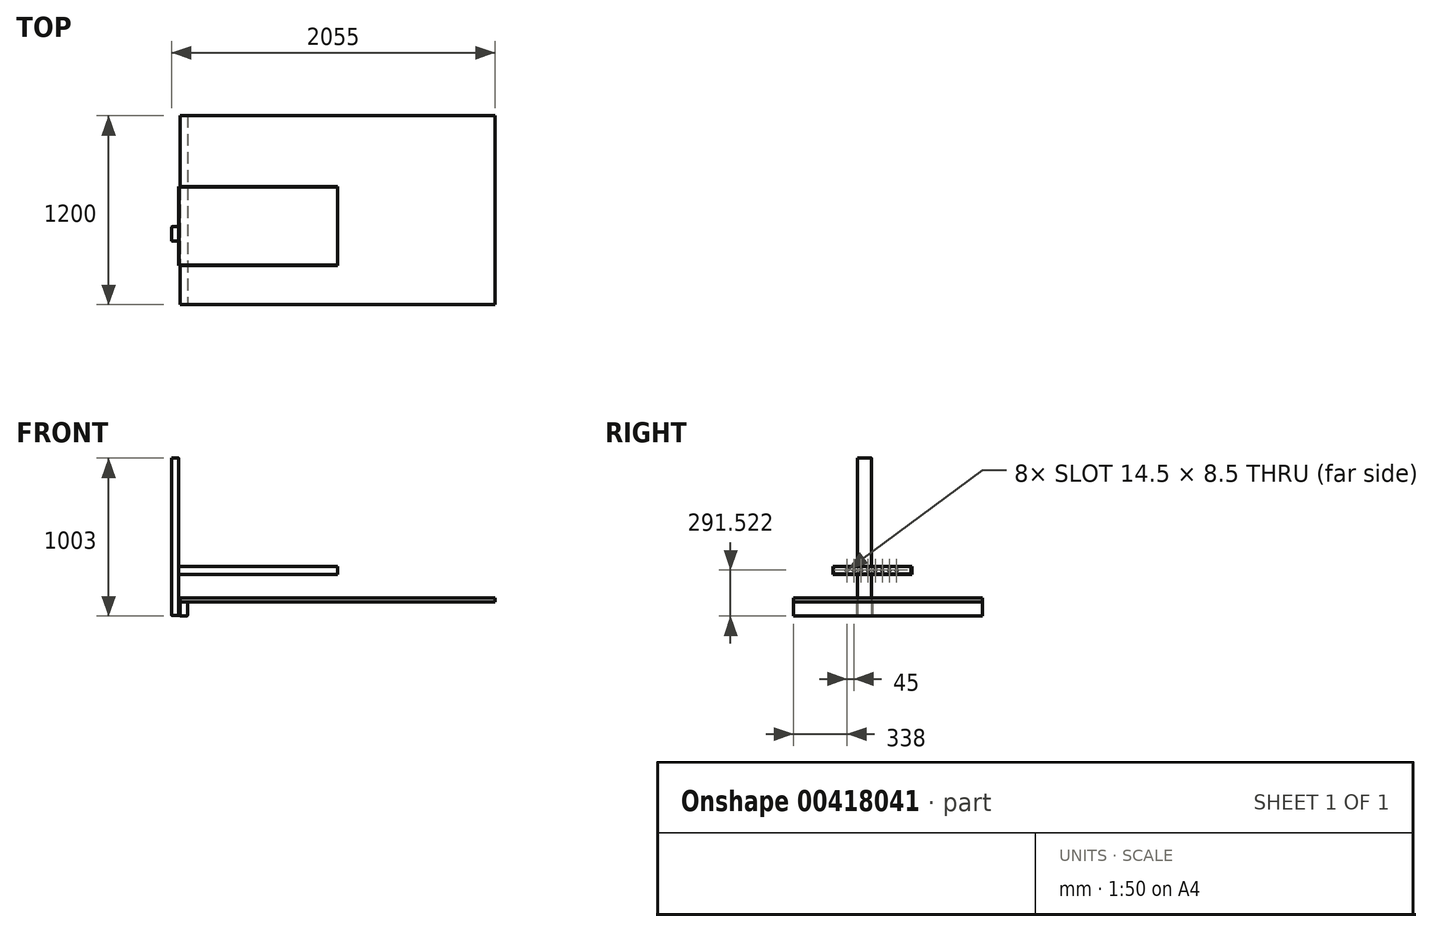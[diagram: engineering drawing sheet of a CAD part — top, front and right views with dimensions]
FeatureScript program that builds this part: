
annotation { "Feature Type Name" : "Feature", "Feature Type Description" : "" }
export const myFeature = defineFeature(function(context is Context, id is Id, definition is map)
    precondition{}
    {
        {
            var Q0;
            Q0=qCreatedBy(makeId("Top.planeOp"),FACE);
            var sketch = newSketch(context, id + "F0", { "sketchPlane" : qUnion([Q0])});
            skLineSegment(sketch, "E0.bottom", {"start": v(-1000, 600) * mm, "end": v(1000, 600) * mm});
            skLineSegment(sketch, "E0.top", {"start": v(-1000, -600) * mm, "end": v(1000, -600) * mm});
            skLineSegment(sketch, "E0.left", {"start": v(-1000, 600) * mm, "end": v(-1000, -600) * mm});
            skLineSegment(sketch, "E0.right", {"start": v(1000, 600) * mm, "end": v(1000, -600) * mm});
            skPoint(sketch, "E0.middle", {"position": v(0, 0) * mm});
            skSolve(sketch);
        }
        {
            var Q0;
            Q0 = qSketchRegion(id + "F0", true);
            extrude(context, id + "F1", {"entities" : qUnion([Q0]), "oppositeDirection" : true, "depth" : 25 * mm});
        }
        {
            var Q0;
            Q0=makeQuery(id+"F1.opExtrude","SWEPT_FACE",FACE,{"disambiguationData":[OSD([sQuery(id+"F0.wireOp",EDGE,"E0.top")])]});
            var sketch = newSketch(context, id + "F2", { "sketchPlane" : qUnion([Q0])});
            skLineSegment(sketch, "E1.bottom", {"start": v(-997, -25) * mm, "end": v(-958, -25) * mm});
            skLineSegment(sketch, "E1.top", {"start": v(-997, -115) * mm, "end": v(-958, -115) * mm});
            skLineSegment(sketch, "E1.left", {"start": v(-1000, -28) * mm, "end": v(-1000, -112) * mm});
            skLineSegment(sketch, "E1.right", {"start": v(-955, -28) * mm, "end": v(-955, -112) * mm});
            skPoint(sketch, "E2.visualSharp", {"position": v(-1000, -115) * mm});
            skArc(sketch, "E2.filletArc", {"start": v(-1000, -112) * mm, "mid": v(-999.12, -114.12) * mm, "end": v(-997, -115) * mm});
            skPoint(sketch, "E3.visualSharp", {"position": v(-1000, -25) * mm});
            skArc(sketch, "E3.filletArc", {"start": v(-997, -25) * mm, "mid": v(-999.12, -25.88) * mm, "end": v(-1000, -28) * mm});
            skPoint(sketch, "E4.visualSharp", {"position": v(-955, -25) * mm});
            skArc(sketch, "E4.filletArc", {"start": v(-955, -28) * mm, "mid": v(-955.88, -25.88) * mm, "end": v(-958, -25) * mm});
            skPoint(sketch, "E5.visualSharp", {"position": v(-955, -115) * mm});
            skArc(sketch, "E5.filletArc", {"start": v(-958, -115) * mm, "mid": v(-955.88, -114.12) * mm, "end": v(-955, -112) * mm});
            skSolve(sketch);
        }
        {
            var Q0;
            Q0=makeQuery(id+"F2.imprint","IMPRINT",FACE,{"disambiguationData":[TD([[makeQuery(id+"F2.imprint","IMPRINT",EDGE,{"derivedFrom":sQuery(id+"F2.wireOp",EDGE,"E1.bottom")}),-1.0]])]});
            extrude(context, id + "F3", {"entities" : qUnion([Q0]), "oppositeDirection" : true, "depth" : 1200 * mm});
        }
        {
            var Q0;
            Q0=qCreatedBy(makeId("Right.planeOp"),FACE);
            var sketch = newSketch(context, id + "F4", { "sketchPlane" : qUnion([Q0])});
            skLineSegment(sketch, "E6.bottom", {"start": v(-618.7, -152.52) * mm, "end": v(618.7, -152.52) * mm});
            skLineSegment(sketch, "E6.top", {"start": v(-618.7, 152.52) * mm, "end": v(618.7, 152.52) * mm});
            skLineSegment(sketch, "E6.left", {"start": v(-618.7, -152.52) * mm, "end": v(-618.7, 152.52) * mm});
            skLineSegment(sketch, "E6.right", {"start": v(618.7, -152.52) * mm, "end": v(618.7, 152.52) * mm});
            skPoint(sketch, "E6.middle", {"position": v(0, 0) * mm});
            skSolve(sketch);
        }
        {
            var Q0;
            Q0=makeQuery(id+"F4.imprint","IMPRINT",FACE,{"disambiguationData":[TD([[makeQuery(id+"F4.imprint","IMPRINT",EDGE,{"derivedFrom":sQuery(id+"F4.wireOp",EDGE,"E6.bottom")}),1.0]])]});
            cPlane(context, id + "F5", {"entities" : qUnion([Q0]), "cplaneType" : CPlaneType.OFFSET, "offset" : 0 * mm, "width" : 150 * mm, "height" : 150 * mm});
        }
        {
            var Q0;
            Q0=makeQuery(id+"F3.opExtrude","SWEPT_FACE",FACE,{"disambiguationData":[OSD([sQuery(id+"F2.wireOp",EDGE,"E1.left")])]});
            var sketch = newSketch(context, id + "F6", { "sketchPlane" : qUnion([Q0])});
            skLineSegment(sketch, "E7.bottom", {"start": v(100, -28) * mm, "end": v(200, -28) * mm});
            skLineSegment(sketch, "E7.top", {"start": v(100, -112) * mm, "end": v(200, -112) * mm});
            skLineSegment(sketch, "E7.left", {"start": v(100, -28) * mm, "end": v(100, -112) * mm});
            skLineSegment(sketch, "E7.right", {"start": v(200, -28) * mm, "end": v(200, -112) * mm});
            skSolve(sketch);
        }
        {
            var Q0;
            Q0=makeQuery(id+"F6.imprint","IMPRINT",FACE,{"disambiguationData":[TD([[makeQuery(id+"F6.imprint","IMPRINT",EDGE,{"derivedFrom":sQuery(id+"F6.wireOp",EDGE,"E7.bottom")}),-1.0]])]});
            extrude(context, id + "F7", {"entities" : qUnion([Q0]), "operationType" : NewBodyOperationType.ADD, "depth" : 10 * mm});
        }
        {
            var Q0;
            Q0=makeQuery(id+"F7.opExtrude","CAP_FACE",FACE,{"disambiguationData":[OSD([sQuery(id+"F6.wireOp",EDGE,"E7.bottom"),sQuery(id+"F6.wireOp",EDGE,"E7.top"),sQuery(id+"F6.wireOp",EDGE,"E7.left"),sQuery(id+"F6.wireOp",EDGE,"E7.right")])],"isStart":false});
            var sketch = newSketch(context, id + "F8", { "sketchPlane" : qUnion([Q0])});
            skLineSegment(sketch, "E8", {"start": v(350, 150.93) * mm, "end": v(-150, 150.93) * mm});
            skLineSegment(sketch, "E9", {"start": v(-150, 150.93) * mm, "end": v(-150, 200.93) * mm});
            skLineSegment(sketch, "E10", {"start": v(350, 150.93) * mm, "end": v(350, 200.93) * mm});
            skLineSegment(sketch, "E11.0", {"start": v(348.5, 152.43) * mm, "end": v(348.5, 200.62) * mm});
            skLineSegment(sketch, "E11.1", {"start": v(348.5, 152.43) * mm, "end": v(-148.5, 152.43) * mm});
            skLineSegment(sketch, "E11.2", {"start": v(-148.5, 152.43) * mm, "end": v(-148.5, 200.93) * mm});
            skLineSegment(sketch, "E12", {"start": v(350, 200.93) * mm, "end": v(348.5, 200.62) * mm});
            skLineSegment(sketch, "E13", {"start": v(-150, 200.93) * mm, "end": v(-148.5, 200.93) * mm});
            skLineSegment(sketch, "E14", {"start": v(-145.24, 152.43) * mm, "end": v(-145.24, 166.43) * mm});
            skLineSegment(sketch, "E15", {"start": v(346.04, 201.52) * mm, "end": v(346.04, 152.43) * mm});
            skLineSegment(sketch, "E16", {"start": v(-145.24, 201.52) * mm, "end": v(346.04, 201.52) * mm});
            skLineSegment(sketch, "E17", {"start": v(362, 176.52) * mm, "end": v(-153.07, 176.52) * mm, "construction": true});
            skPoint(sketch, "E17.startSnap0", {"position": v(348.5, 176.52) * mm});
            skArc(sketch, "E18", {"start": v(-56, 180.77) * mm, "mid": v(-60.25, 176.52) * mm, "end": v(-56, 172.27) * mm});
            skArc(sketch, "E19", {"start": v(-50, 172.27) * mm, "mid": v(-45.75, 176.52) * mm, "end": v(-50, 180.77) * mm});
            skLineSegment(sketch, "E20", {"start": v(-56, 180.77) * mm, "end": v(-50, 180.77) * mm});
            skLineSegment(sketch, "E21", {"start": v(-56, 172.27) * mm, "end": v(-50, 172.27) * mm});
            skArc(sketch, "E22.1.0.0", {"start": v(-5, 172.27) * mm, "mid": v(-0.75, 176.52) * mm, "end": v(-5, 180.77) * mm});
            skLineSegment(sketch, "E22.1.0.1", {"start": v(-11, 180.77) * mm, "end": v(-5, 180.77) * mm});
            skArc(sketch, "E22.1.0.2", {"start": v(-11, 180.77) * mm, "mid": v(-15.25, 176.52) * mm, "end": v(-11, 172.27) * mm});
            skLineSegment(sketch, "E22.1.0.3", {"start": v(-11, 172.27) * mm, "end": v(-5, 172.27) * mm});
            skArc(sketch, "E22.2.0.0", {"start": v(40, 172.27) * mm, "mid": v(44.25, 176.52) * mm, "end": v(40, 180.77) * mm});
            skLineSegment(sketch, "E22.2.0.1", {"start": v(34, 180.77) * mm, "end": v(40, 180.77) * mm});
            skArc(sketch, "E22.2.0.2", {"start": v(34, 180.77) * mm, "mid": v(29.75, 176.52) * mm, "end": v(34, 172.27) * mm});
            skLineSegment(sketch, "E22.2.0.3", {"start": v(34, 172.27) * mm, "end": v(40, 172.27) * mm});
            skArc(sketch, "E22.3.0.0", {"start": v(85, 172.27) * mm, "mid": v(89.25, 176.52) * mm, "end": v(85, 180.77) * mm});
            skLineSegment(sketch, "E22.3.0.1", {"start": v(79, 180.77) * mm, "end": v(85, 180.77) * mm});
            skArc(sketch, "E22.3.0.2", {"start": v(79, 180.77) * mm, "mid": v(74.75, 176.52) * mm, "end": v(79, 172.27) * mm});
            skLineSegment(sketch, "E22.3.0.3", {"start": v(79, 172.27) * mm, "end": v(85, 172.27) * mm});
            skArc(sketch, "E22.4.0.0", {"start": v(130, 172.27) * mm, "mid": v(134.25, 176.52) * mm, "end": v(130, 180.77) * mm});
            skLineSegment(sketch, "E22.4.0.1", {"start": v(124, 180.77) * mm, "end": v(130, 180.77) * mm});
            skArc(sketch, "E22.4.0.2", {"start": v(124, 180.77) * mm, "mid": v(119.75, 176.52) * mm, "end": v(124, 172.27) * mm});
            skLineSegment(sketch, "E22.4.0.3", {"start": v(124, 172.27) * mm, "end": v(130, 172.27) * mm});
            skArc(sketch, "E22.5.0.0", {"start": v(175, 172.27) * mm, "mid": v(179.25, 176.52) * mm, "end": v(175, 180.77) * mm});
            skLineSegment(sketch, "E22.5.0.1", {"start": v(169, 180.77) * mm, "end": v(175, 180.77) * mm});
            skArc(sketch, "E22.5.0.2", {"start": v(169, 180.77) * mm, "mid": v(164.75, 176.52) * mm, "end": v(169, 172.27) * mm});
            skLineSegment(sketch, "E22.5.0.3", {"start": v(169, 172.27) * mm, "end": v(175, 172.27) * mm});
            skArc(sketch, "E22.6.0.0", {"start": v(220, 172.27) * mm, "mid": v(224.25, 176.52) * mm, "end": v(220, 180.77) * mm});
            skLineSegment(sketch, "E22.6.0.1", {"start": v(214, 180.77) * mm, "end": v(220, 180.77) * mm});
            skArc(sketch, "E22.6.0.2", {"start": v(214, 180.77) * mm, "mid": v(209.75, 176.52) * mm, "end": v(214, 172.27) * mm});
            skLineSegment(sketch, "E22.6.0.3", {"start": v(214, 172.27) * mm, "end": v(220, 172.27) * mm});
            skArc(sketch, "E22.7.0.0", {"start": v(265, 172.27) * mm, "mid": v(269.25, 176.52) * mm, "end": v(265, 180.77) * mm});
            skLineSegment(sketch, "E22.7.0.1", {"start": v(259, 180.77) * mm, "end": v(265, 180.77) * mm});
            skArc(sketch, "E22.7.0.2", {"start": v(259, 180.77) * mm, "mid": v(254.75, 176.52) * mm, "end": v(259, 172.27) * mm});
            skLineSegment(sketch, "E22.7.0.3", {"start": v(259, 172.27) * mm, "end": v(265, 172.27) * mm});
            skLineSegment(sketch, "E22.direction1", {"start": v(-50, 172.27) * mm, "end": v(-5, 172.27) * mm, "construction": true});
            skLineSegment(sketch, "E23", {"start": v(-145.24, 166.43) * mm, "end": v(-145.24, 201.52) * mm});
            skSolve(sketch);
        }
        {
            var Q0;
            {var subQ0=sQuery(id+"F8.wireOp",EDGE,"E14");Q0=makeQuery(id+"F8.imprint","IMPRINT",FACE,{"disambiguationData":[TD([[makeQuery(id+"F8.imprint","IMPRINT",EDGE,{"derivedFrom":subQ0}),-1.0]])]});}
            var Q1;
            Q1=makeQuery(id+"F8.imprint","IMPRINT",FACE,{"disambiguationData":[TD([[makeQuery(id+"F8.imprint","IMPRINT",EDGE,{"derivedFrom":sQuery(id+"F8.wireOp",EDGE,"E22.4.0.0")}),-1.0]])]});
            var Q2;
            {var subQ5=sQuery(id+"F8.wireOp",EDGE,"E15");Q2=makeQuery(id+"F8.imprint","IMPRINT",FACE,{"disambiguationData":[TD([[makeQuery(id+"F8.imprint","IMPRINT",EDGE,{"derivedFrom":subQ5}),-1.0]])]});}
            extrude(context, id + "F9", {"entities" : qUnion([Q0, Q1, Q2]), "oppositeDirection" : true, "depth" : 1.5 * mm});
        }
        {
            var Q0;
            Q0=makeQuery(id+"F8.imprint","IMPRINT",FACE,{"disambiguationData":[TD([[makeQuery(id+"F8.imprint","IMPRINT",EDGE,{"derivedFrom":sQuery(id+"F8.wireOp",EDGE,"E8")}),-1.0]])]});
            var Q1;
            {var subQ0=sQuery(id+"F8.wireOp",EDGE,"E10");Q1=makeQuery(id+"F8.imprint","IMPRINT",FACE,{"disambiguationData":[TD([[makeQuery(id+"F8.imprint","IMPRINT",EDGE,{"derivedFrom":subQ0}),1.0]])]});}
            var Q2;
            {var subQ4=sQuery(id+"F8.wireOp",EDGE,"E9");Q2=makeQuery(id+"F8.imprint","IMPRINT",FACE,{"disambiguationData":[TD([[makeQuery(id+"F8.imprint","IMPRINT",EDGE,{"derivedFrom":subQ4}),-1.0]])]});}
            var Q3;
            Q3=qCreatedBy(id+"F5.planeOp",FACE);
            extrude(context, id + "F10", {"entities" : qUnion([Q0, Q1, Q2]), "endBound" : BoundingType.UP_TO_SURFACE, "oppositeDirection" : true, "endBoundEntityFace" : qUnion([Q3]), "depth" : 300 * mm});
        }
        {
            var Q0;
            Q0=makeQuery(id+"F7.opExtrude","SWEPT_FACE",FACE,{"disambiguationData":[OSD([sQuery(id+"F6.wireOp",EDGE,"E7.top")])]});
            var sketch = newSketch(context, id + "F11", { "sketchPlane" : qUnion([Q0])});
            skLineSegment(sketch, "E24.bottom", {"start": v(-1013, 195) * mm, "end": v(-1052, 195) * mm});
            skLineSegment(sketch, "E24.top", {"start": v(-1013, 105) * mm, "end": v(-1052, 105) * mm});
            skLineSegment(sketch, "E24.left", {"start": v(-1010, 192) * mm, "end": v(-1010, 108) * mm});
            skLineSegment(sketch, "E24.right", {"start": v(-1055, 192) * mm, "end": v(-1055, 108) * mm});
            skPoint(sketch, "E25.visualSharp", {"position": v(-1055, 195) * mm});
            skArc(sketch, "E25.filletArc", {"start": v(-1052, 195) * mm, "mid": v(-1054.12, 194.12) * mm, "end": v(-1055, 192) * mm});
            skPoint(sketch, "E26.visualSharp", {"position": v(-1010, 195) * mm});
            skArc(sketch, "E26.filletArc", {"start": v(-1010, 192) * mm, "mid": v(-1010.88, 194.12) * mm, "end": v(-1013, 195) * mm});
            skPoint(sketch, "E27.visualSharp", {"position": v(-1010, 105) * mm});
            skArc(sketch, "E27.filletArc", {"start": v(-1013, 105) * mm, "mid": v(-1010.88, 105.88) * mm, "end": v(-1010, 108) * mm});
            skPoint(sketch, "E28.visualSharp", {"position": v(-1055, 105) * mm});
            skArc(sketch, "E28.filletArc", {"start": v(-1055, 108) * mm, "mid": v(-1054.12, 105.88) * mm, "end": v(-1052, 105) * mm});
            skSolve(sketch);
        }
        {
            var Q0;
            Q0=makeQuery(id+"F11.imprint","IMPRINT",FACE,{"disambiguationData":[TD([[makeQuery(id+"F11.imprint","IMPRINT",EDGE,{"derivedFrom":sQuery(id+"F11.wireOp",EDGE,"E24.bottom")}),1.0]])]});
            extrude(context, id + "F12", {"entities" : qUnion([Q0]), "oppositeDirection" : true, "depth" : 1000 * mm});
        }
    });
